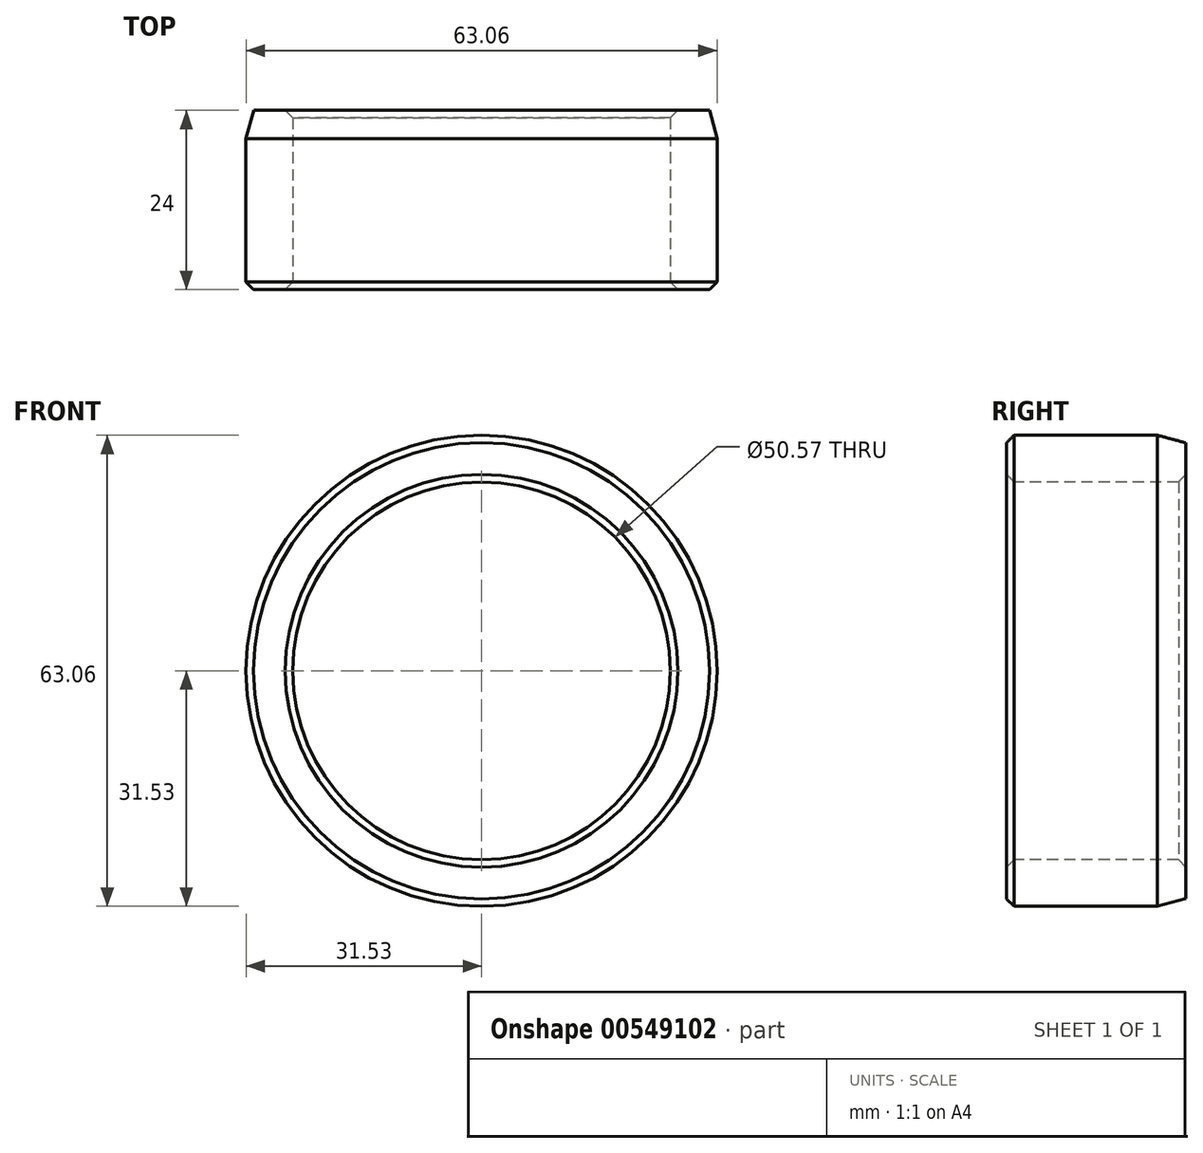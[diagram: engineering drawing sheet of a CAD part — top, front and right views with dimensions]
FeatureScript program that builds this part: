
annotation { "Feature Type Name" : "Feature", "Feature Type Description" : "" }
export const myFeature = defineFeature(function(context is Context, id is Id, definition is map)
    precondition{}
    {
        {
            var Q0;
            Q0=qCreatedBy(makeId("Right.planeOp"),FACE);
            var sketch = newSketch(context, id + "F0", { "sketchPlane" : qUnion([Q0])});
            skLineSegment(sketch, "E0.bottom", {"start": v(0, 31.53) * mm, "end": v(24, 31.53) * mm});
            skLineSegment(sketch, "E0.top", {"start": v(0, 25.29) * mm, "end": v(24, 25.29) * mm});
            skLineSegment(sketch, "E0.left", {"start": v(0, 31.53) * mm, "end": v(0, 25.29) * mm});
            skLineSegment(sketch, "E0.right", {"start": v(24, 31.53) * mm, "end": v(24, 25.29) * mm});
            skLineSegment(sketch, "E1", {"start": v(0, 0) * mm, "end": v(20.14, 0) * mm, "construction": true});
            skSolve(sketch);
        }
        {
            var Q0;
            Q0=makeQuery(id+"F0.imprint","IMPRINT",FACE,{"disambiguationData":[TD([[makeQuery(id+"F0.imprint","IMPRINT",EDGE,{"derivedFrom":sQuery(id+"F0.wireOp",EDGE,"E0.bottom")}),-1.0]])]});
            var Q1;
            Q1=sQuery(id+"F0.wireOp",EDGE,"E1");
            revolve(context, id + "F1", {"entities" : qUnion([Q0]), "axis" : qUnion([Q1]), "revolveType" : RevolveType.FULL});
        }
        {
            var Q0;
            Q0=makeQuery(id+"F1.opRevolve","SWEPT_EDGE",EDGE,{"disambiguationData":[OSD([sQuery(id+"F0.wireOp",EDGE,"E0.top"),sQuery(id+"F0.wireOp",EDGE,"E0.left")])]});
            var Q1;
            Q1=makeQuery(id+"F1.opRevolve","SWEPT_EDGE",EDGE,{"disambiguationData":[OSD([sQuery(id+"F0.wireOp",EDGE,"E0.bottom"),sQuery(id+"F0.wireOp",EDGE,"E0.left")])]});
            var Q2;
            Q2=makeQuery(id+"F1.opRevolve","SWEPT_EDGE",EDGE,{"disambiguationData":[OSD([sQuery(id+"F0.wireOp",EDGE,"E0.top"),sQuery(id+"F0.wireOp",EDGE,"E0.right")])]});
            chamfer(context, id + "F2", {"entities" : qUnion([Q0, Q1, Q2]), "width" : 1 * mm, "tangentPropagation" : true});
        }
        {
            var Q0;
            Q0=makeQuery(id+"F1.opRevolve","SWEPT_EDGE",EDGE,{"disambiguationData":[OSD([sQuery(id+"F0.wireOp",EDGE,"E0.bottom"),sQuery(id+"F0.wireOp",EDGE,"E0.right")])]});
            chamfer(context, id + "F3", {"entities" : qUnion([Q0]), "chamferType" : ChamferType.OFFSET_ANGLE, "width" : 3.8 * mm, "oppositeDirection" : false, "angle" : 15 * degree, "tangentPropagation" : true});
        }
    });
